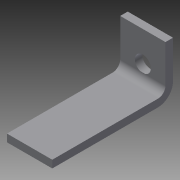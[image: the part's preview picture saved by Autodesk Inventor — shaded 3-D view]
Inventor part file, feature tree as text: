
AUTODESK INVENTOR PART (.ipt)
format: ipt  version: 2013 (Build 170138000, 138)  size: 115,200 bytes
history: native  units: in
note: dims shown in document units (in); Inventor stores cm internally (conversion verified against a paired STEP export)
features: sheet_metal_op x4, sketch x4, other x4, reference x3
ambient origin geometry x8: Origin, YZ Plane, XZ Plane, XY Plane, X Axis, Y Axis, Z Axis, Center Point
bodies: Solid1 (feature_tree)
feature tree (15):
  sheet_metal_op  "Face1"
  sheet_metal_op  "Flange1"
  sketch  "Sketch1"  dims[d0=0.875in]
  other  "Plate1"
  sketch  "Sketch2"  dims[d1=0.75in]
  other  "Plate2"
  sheet_metal_op  "Bend1"
  sheet_metal_op  "Corner1"
  sketch  "Sketch3"  dims[d2=0.125in]
  reference  "Reference1"
  reference  "Reference2"
  reference  "Reference3"
  sketch  "Sketch4"  dims[d3=0.125in d4=0.0625in d5=0.25in d6=0.125in d7=3.0in d8=90.0deg d9=0.05in d10=0.5in d11=0.125in d12=0.125in d13=0.125in d14=0.0in d15=0.5in d16=0.266in d17=0.5in d18=0.266in d19=0.125in d20=0.0in]
  other  "Cut1"
  other  "Cut2"
